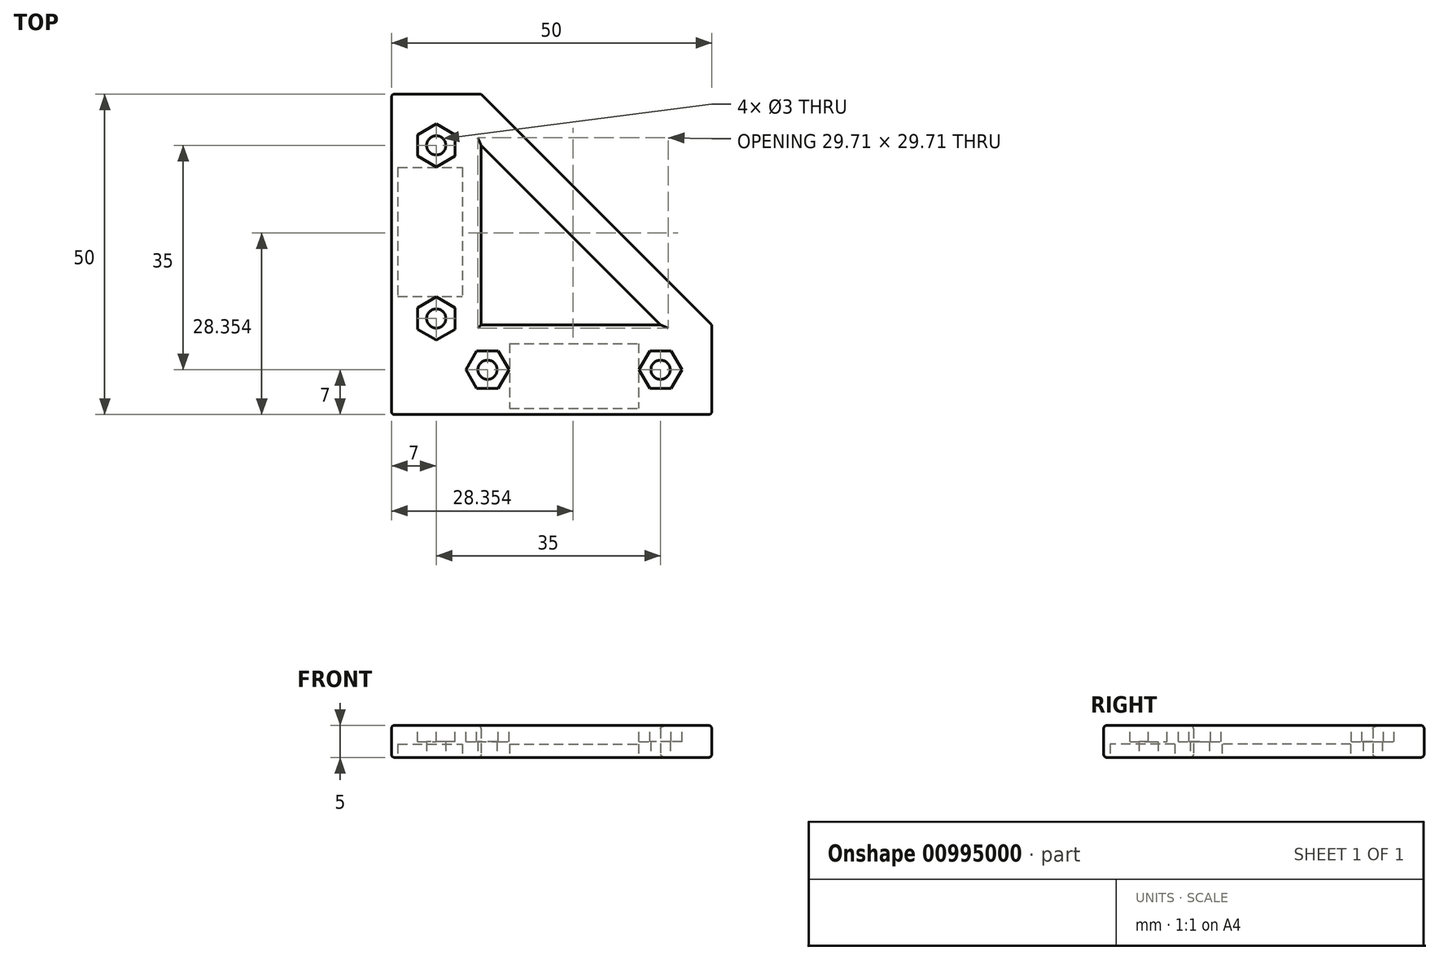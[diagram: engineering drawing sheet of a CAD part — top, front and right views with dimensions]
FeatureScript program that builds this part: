
annotation { "Feature Type Name" : "Feature", "Feature Type Description" : "" }
export const myFeature = defineFeature(function(context is Context, id is Id, definition is map)
    precondition{}
    {
        {
            var Q0;
            Q0=qCreatedBy(makeId("Top.planeOp"),FACE);
            var sketch = newSketch(context, id + "F0", { "sketchPlane" : qUnion([Q0])});
            skLineSegment(sketch, "E0.bottom", {"start": v(0, 0) * mm, "end": v(50, 0) * mm});
            skLineSegment(sketch, "E0.top", {"start": v(0, 50) * mm, "end": v(50, 50) * mm});
            skLineSegment(sketch, "E0.left", {"start": v(0, 0) * mm, "end": v(0, 50) * mm});
            skLineSegment(sketch, "E0.right", {"start": v(50, 0) * mm, "end": v(50, 50) * mm});
            skLineSegment(sketch, "E1", {"start": v(14, 50) * mm, "end": v(50, 14) * mm});
            skLineSegment(sketch, "E2", {"start": v(14, 50) * mm, "end": v(14, 14) * mm});
            skLineSegment(sketch, "E3", {"start": v(14, 14) * mm, "end": v(50, 14) * mm});
            skLineSegment(sketch, "E4", {"start": v(50, 7) * mm, "end": v(0, 7) * mm, "construction": true});
            skLineSegment(sketch, "E5", {"start": v(7, 0) * mm, "end": v(7, 50) * mm, "construction": true});
            skPoint(sketch, "E6", {"position": v(7, 42) * mm});
            skPoint(sketch, "E7", {"position": v(7, 15) * mm});
            skPoint(sketch, "E8", {"position": v(42, 7) * mm});
            skPoint(sketch, "E9", {"position": v(15, 7) * mm});
            skLineSegment(sketch, "E10", {"start": v(14, 14) * mm, "end": v(0, 0) * mm, "construction": true});
            skLineSegment(sketch, "E11.bottom", {"start": v(1, 38.55) * mm, "end": v(11.1, 38.55) * mm});
            skLineSegment(sketch, "E11.top", {"start": v(1, 18.45) * mm, "end": v(11.1, 18.45) * mm});
            skLineSegment(sketch, "E11.left", {"start": v(1, 38.55) * mm, "end": v(1, 18.45) * mm});
            skLineSegment(sketch, "E11.right", {"start": v(11.1, 38.55) * mm, "end": v(11.1, 18.45) * mm});
            skLineSegment(sketch, "E12.bottom", {"start": v(18.45, 11.1) * mm, "end": v(38.55, 11.1) * mm});
            skLineSegment(sketch, "E12.top", {"start": v(18.45, 1) * mm, "end": v(38.55, 1) * mm});
            skLineSegment(sketch, "E12.left", {"start": v(18.45, 11.1) * mm, "end": v(18.45, 1) * mm});
            skLineSegment(sketch, "E12.right", {"start": v(38.55, 11.1) * mm, "end": v(38.55, 1) * mm});
            skLineSegment(sketch, "E13", {"start": v(1, 28.5) * mm, "end": v(11.1, 28.5) * mm, "construction": true});
            skLineSegment(sketch, "E14", {"start": v(28.5, 11.1) * mm, "end": v(28.5, 1) * mm, "construction": true});
            skLineSegment(sketch, "E15", {"start": v(14, 42) * mm, "end": v(42, 14) * mm});
            skSolve(sketch);
        }
        {
            var Q0;
            {var subQ11=sQuery(id+"F0.wireOp",EDGE,"E0.bottom");Q0=makeQuery(id+"F0.imprint","IMPRINT",FACE,{"disambiguationData":[TD([[makeQuery(id+"F0.imprint","IMPRINT",EDGE,{"derivedFrom":subQ11}),1.0]])]});}
            var Q1;
            {var subQ0=sQuery(id+"F0.wireOp",EDGE,"E1");Q1=makeQuery(id+"F0.imprint","IMPRINT",FACE,{"disambiguationData":[TD([[makeQuery(id+"F0.imprint","IMPRINT",EDGE,{"derivedFrom":subQ0}),-1.0]])]});}
            var Q2;
            Q2=makeQuery(id+"F0.imprint","IMPRINT",FACE,{"disambiguationData":[TD([[makeQuery(id+"F0.imprint","IMPRINT",EDGE,{"derivedFrom":sQuery(id+"F0.wireOp",EDGE,"E11.bottom")}),-1.0]])]});
            var Q3;
            Q3=makeQuery(id+"F0.imprint","IMPRINT",FACE,{"disambiguationData":[TD([[makeQuery(id+"F0.imprint","IMPRINT",EDGE,{"derivedFrom":sQuery(id+"F0.wireOp",EDGE,"E12.bottom")}),-1.0]])]});
            extrude(context, id + "F1", {"entities" : qUnion([Q0, Q1, Q2, Q3]), "depth" : 5 * mm, "offsetDistance" : 25 * mm});
        }
        {
            var Q0;
            Q0=makeQuery(id+"F0.imprint","IMPRINT",FACE,{"disambiguationData":[TD([[makeQuery(id+"F0.imprint","IMPRINT",EDGE,{"derivedFrom":sQuery(id+"F0.wireOp",EDGE,"E11.bottom")}),-1.0]])]});
            var Q1;
            Q1=makeQuery(id+"F0.imprint","IMPRINT",FACE,{"disambiguationData":[TD([[makeQuery(id+"F0.imprint","IMPRINT",EDGE,{"derivedFrom":sQuery(id+"F0.wireOp",EDGE,"E12.bottom")}),-1.0]])]});
            extrude(context, id + "F2", {"entities" : qUnion([Q0, Q1]), "operationType" : NewBodyOperationType.REMOVE, "depth" : 2.1 * mm, "offsetDistance" : 25 * mm});
        }
        {
            var Q0;
            Q0=sQuery(id+"F0.wireOp",VERTEX,"E7");
            var Q1;
            Q1=sQuery(id+"F0.wireOp",VERTEX,"E9");
            var Q2;
            Q2=sQuery(id+"F0.wireOp",VERTEX,"E8");
            var Q3;
            Q3=sQuery(id+"F0.wireOp",VERTEX,"E6");
            var Q4;
            Q4=makeQuery(id+"F1.opExtrude","SWEPT_BODY",BODY,{"disambiguationData":[OSD([sQuery(id+"F0.wireOp",EDGE,"E0.bottom"),sQuery(id+"F0.wireOp",EDGE,"E0.top"),sQuery(id+"F0.wireOp",EDGE,"E0.left"),sQuery(id+"F0.wireOp",EDGE,"E0.right"),sQuery(id+"F0.wireOp",EDGE,"E1"),sQuery(id+"F0.wireOp",EDGE,"E2"),sQuery(id+"F0.wireOp",EDGE,"E3"),sQuery(id+"F0.wireOp",EDGE,"E15")])]});
            hole(context, id + "F3", {"style" : HoleStyle.SIMPLE, "endStyle" : HoleEndStyle.THROUGH, "oppositeDirection" : true, "holeDiameter" : 3 * mm, "majorDiameter" : 5 * mm, "isTappedThrough" : true, "tappedDepth" : 12 * mm, "tapClearance" : 3, "locations" : qUnion([Q0, Q1, Q2, Q3]), "scope" : qUnion([Q4])});
        }
        {
            var Q0;
            Q0=makeQuery(id+"F1.opExtrude","CAP_FACE",FACE,{"disambiguationData":[OSD([sQuery(id+"F0.wireOp",EDGE,"E0.bottom"),sQuery(id+"F0.wireOp",EDGE,"E0.top"),sQuery(id+"F0.wireOp",EDGE,"E0.left"),sQuery(id+"F0.wireOp",EDGE,"E0.right"),sQuery(id+"F0.wireOp",EDGE,"E1"),sQuery(id+"F0.wireOp",EDGE,"E2"),sQuery(id+"F0.wireOp",EDGE,"E3"),sQuery(id+"F0.wireOp",EDGE,"E15")])],"isStart":false});
            var sketch = newSketch(context, id + "F4", { "sketchPlane" : qUnion([Q0])});
            skCircle(sketch, "E16.cCircle", {"center": v(7, 42) * mm, "radius": 2.9 * mm, "construction": true});
            skLineSegment(sketch, "E16.0", {"start": v(4.1, 43.67) * mm, "end": v(7, 45.35) * mm});
            skLineSegment(sketch, "E16.1", {"start": v(7, 45.35) * mm, "end": v(9.9, 43.67) * mm});
            skLineSegment(sketch, "E16.2", {"start": v(9.9, 43.67) * mm, "end": v(9.9, 40.33) * mm});
            skLineSegment(sketch, "E16.3", {"start": v(9.9, 40.33) * mm, "end": v(7, 38.65) * mm});
            skLineSegment(sketch, "E16.4", {"start": v(7, 38.65) * mm, "end": v(4.1, 40.33) * mm});
            skLineSegment(sketch, "E16.5", {"start": v(4.1, 40.33) * mm, "end": v(4.1, 43.67) * mm});
            skPoint(sketch, "E16.0.midPoint", {"position": v(5.55, 44.51) * mm});
            skCircle(sketch, "E17.cCircle", {"center": v(7, 15) * mm, "radius": 2.9 * mm, "construction": true});
            skLineSegment(sketch, "E17.0", {"start": v(4.1, 16.67) * mm, "end": v(7, 18.35) * mm});
            skLineSegment(sketch, "E17.1", {"start": v(7, 18.35) * mm, "end": v(9.9, 16.67) * mm});
            skLineSegment(sketch, "E17.2", {"start": v(9.9, 16.67) * mm, "end": v(9.9, 13.33) * mm});
            skLineSegment(sketch, "E17.3", {"start": v(9.9, 13.33) * mm, "end": v(7, 11.65) * mm});
            skLineSegment(sketch, "E17.4", {"start": v(7, 11.65) * mm, "end": v(4.1, 13.33) * mm});
            skLineSegment(sketch, "E17.5", {"start": v(4.1, 13.33) * mm, "end": v(4.1, 16.67) * mm});
            skPoint(sketch, "E17.0.midPoint", {"position": v(5.55, 17.51) * mm});
            skCircle(sketch, "E18.cCircle", {"center": v(15, 7) * mm, "radius": 2.9 * mm, "construction": true});
            skLineSegment(sketch, "E18.0", {"start": v(16.67, 9.9) * mm, "end": v(18.35, 7) * mm});
            skLineSegment(sketch, "E18.1", {"start": v(18.35, 7) * mm, "end": v(16.67, 4.1) * mm});
            skLineSegment(sketch, "E18.2", {"start": v(16.67, 4.1) * mm, "end": v(13.33, 4.1) * mm});
            skLineSegment(sketch, "E18.3", {"start": v(13.33, 4.1) * mm, "end": v(11.65, 7) * mm});
            skLineSegment(sketch, "E18.4", {"start": v(11.65, 7) * mm, "end": v(13.33, 9.9) * mm});
            skLineSegment(sketch, "E18.5", {"start": v(13.33, 9.9) * mm, "end": v(16.67, 9.9) * mm});
            skPoint(sketch, "E18.0.midPoint", {"position": v(17.51, 8.45) * mm});
            skCircle(sketch, "E19.cCircle", {"center": v(42, 7) * mm, "radius": 2.9 * mm, "construction": true});
            skLineSegment(sketch, "E19.0", {"start": v(38.65, 7) * mm, "end": v(40.33, 9.9) * mm});
            skLineSegment(sketch, "E19.1", {"start": v(40.33, 9.9) * mm, "end": v(43.67, 9.9) * mm});
            skLineSegment(sketch, "E19.2", {"start": v(43.67, 9.9) * mm, "end": v(45.35, 7) * mm});
            skLineSegment(sketch, "E19.3", {"start": v(45.35, 7) * mm, "end": v(43.67, 4.1) * mm});
            skLineSegment(sketch, "E19.4", {"start": v(43.67, 4.1) * mm, "end": v(40.33, 4.1) * mm});
            skLineSegment(sketch, "E19.5", {"start": v(40.33, 4.1) * mm, "end": v(38.65, 7) * mm});
            skPoint(sketch, "E19.0.midPoint", {"position": v(39.49, 8.45) * mm});
            skSolve(sketch);
        }
        {
            var Q0;
            Q0 = qSketchRegion(id + "F4", true);
            extrude(context, id + "F5", {"entities" : qUnion([Q0]), "operationType" : NewBodyOperationType.REMOVE, "oppositeDirection" : true, "depth" : 2.5 * mm, "offsetDistance" : 25 * mm});
        }
        {
            var Q0;
            Q0=makeQuery(id+"F1.opExtrude","SWEPT_EDGE",EDGE,{"disambiguationData":[OSD([sQuery(id+"F0.wireOp",EDGE,"E0.bottom"),sQuery(id+"F0.wireOp",EDGE,"E0.left")])]});
            var Q1;
            Q1=makeQuery(id+"F1.opExtrude","SWEPT_EDGE",EDGE,{"disambiguationData":[OSD([sQuery(id+"F0.wireOp",EDGE,"E0.bottom"),sQuery(id+"F0.wireOp",EDGE,"E0.right")])]});
            var Q2;
            Q2=makeQuery(id+"F1.opExtrude","SWEPT_EDGE",EDGE,{"disambiguationData":[OSD([sQuery(id+"F0.wireOp",EDGE,"E0.right"),sQuery(id+"F0.wireOp",EDGE,"E1"),sQuery(id+"F0.wireOp",EDGE,"E3")])]});
            var Q3;
            Q3=makeQuery(id+"F1.opExtrude","SWEPT_EDGE",EDGE,{"disambiguationData":[OSD([sQuery(id+"F0.wireOp",EDGE,"E0.top"),sQuery(id+"F0.wireOp",EDGE,"E1"),sQuery(id+"F0.wireOp",EDGE,"E2")])]});
            var Q4;
            Q4=makeQuery(id+"F1.opExtrude","SWEPT_EDGE",EDGE,{"disambiguationData":[OSD([sQuery(id+"F0.wireOp",EDGE,"E0.top"),sQuery(id+"F0.wireOp",EDGE,"E0.left")])]});
            var Q5;
            Q5=makeQuery(id+"F1.opExtrude","CAP_EDGE",EDGE,{"disambiguationData":[OSD([sQuery(id+"F0.wireOp",EDGE,"E0.left")])],"isStart":false});
            var Q6;
            Q6=makeQuery(id+"F1.opExtrude","CAP_EDGE",EDGE,{"disambiguationData":[OSD([sQuery(id+"F0.wireOp",EDGE,"E0.top")])],"isStart":true});
            var Q7;
            Q7=makeQuery(id+"F1.opExtrude","CAP_EDGE",EDGE,{"disambiguationData":[OSD([sQuery(id+"F0.wireOp",EDGE,"E1")])],"isStart":true});
            var Q8;
            Q8=makeQuery(id+"F1.opExtrude","CAP_EDGE",EDGE,{"disambiguationData":[OSD([sQuery(id+"F0.wireOp",EDGE,"E0.right")])],"isStart":true});
            var Q9;
            Q9=makeQuery(id+"F1.opExtrude","CAP_EDGE",EDGE,{"disambiguationData":[OSD([sQuery(id+"F0.wireOp",EDGE,"E0.bottom")])],"isStart":true});
            var Q10;
            Q10=makeQuery(id+"F1.opExtrude","CAP_EDGE",EDGE,{"disambiguationData":[OSD([sQuery(id+"F0.wireOp",EDGE,"E3")])],"isStart":true});
            var Q11;
            Q11=makeQuery(id+"F1.opExtrude","CAP_EDGE",EDGE,{"disambiguationData":[OSD([sQuery(id+"F0.wireOp",EDGE,"E15")])],"isStart":true});
            var Q12;
            Q12=makeQuery(id+"F1.opExtrude","CAP_EDGE",EDGE,{"disambiguationData":[OSD([sQuery(id+"F0.wireOp",EDGE,"E2")])],"isStart":true});
            var Q13;
            Q13=makeQuery(id+"F1.opExtrude","CAP_EDGE",EDGE,{"disambiguationData":[OSD([sQuery(id+"F0.wireOp",EDGE,"E0.left")])],"isStart":true});
            var Q14;
            Q14=makeQuery(id+"F1.opExtrude","CAP_EDGE",EDGE,{"disambiguationData":[OSD([sQuery(id+"F0.wireOp",EDGE,"E0.bottom")])],"isStart":false});
            var Q15;
            Q15=makeQuery(id+"F1.opExtrude","CAP_EDGE",EDGE,{"disambiguationData":[OSD([sQuery(id+"F0.wireOp",EDGE,"E0.right")])],"isStart":false});
            var Q16;
            Q16=makeQuery(id+"F1.opExtrude","CAP_EDGE",EDGE,{"disambiguationData":[OSD([sQuery(id+"F0.wireOp",EDGE,"E1")])],"isStart":false});
            var Q17;
            Q17=makeQuery(id+"F1.opExtrude","CAP_EDGE",EDGE,{"disambiguationData":[OSD([sQuery(id+"F0.wireOp",EDGE,"E2")])],"isStart":false});
            var Q18;
            Q18=makeQuery(id+"F1.opExtrude","CAP_EDGE",EDGE,{"disambiguationData":[OSD([sQuery(id+"F0.wireOp",EDGE,"E15")])],"isStart":false});
            var Q19;
            Q19=makeQuery(id+"F1.opExtrude","CAP_EDGE",EDGE,{"disambiguationData":[OSD([sQuery(id+"F0.wireOp",EDGE,"E3")])],"isStart":false});
            var Q20;
            Q20=makeQuery(id+"F1.opExtrude","CAP_EDGE",EDGE,{"disambiguationData":[OSD([sQuery(id+"F0.wireOp",EDGE,"E0.top")])],"isStart":false});
            fillet(context, id + "F6", {"entities" : qUnion([Q0, Q1, Q2, Q3, Q4, Q5, Q6, Q7, Q8, Q9, Q10, Q11, Q12, Q13, Q14, Q15, Q16, Q17, Q18, Q19, Q20]), "radius" : 0.5 * mm, "tangentPropagation" : true, "allowEdgeOverflow" : false});
        }
    });
